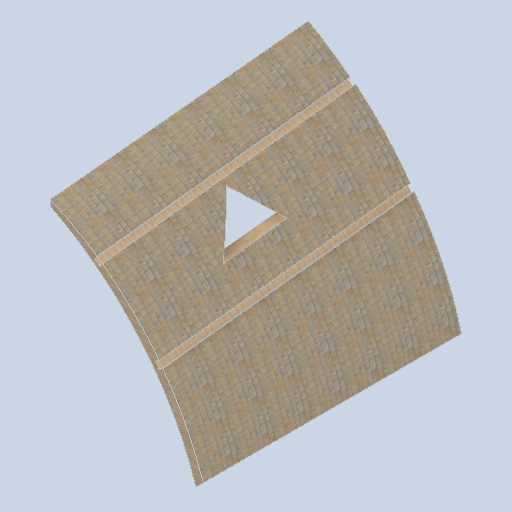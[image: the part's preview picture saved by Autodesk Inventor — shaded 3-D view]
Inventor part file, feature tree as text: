
AUTODESK INVENTOR PART (.ipt)
format: ipt  version: 2024.2 (Build 282272000, 272)  size: 378,368 bytes
history: native  units: in
note: dims shown in document units (in); Inventor stores cm internally (conversion verified against a paired STEP export)
features: other x3, sketch x2, plane x2
ambient origin geometry x8: Origin, YZ Plane, XZ Plane, XY Plane, X Axis, Y Axis, Z Axis, Center Point
bodies: Solid1 (feature_tree)
feature tree (7):
  other  "panel_block_02_MIR.ipt"
  other  "Solid1::panel_block_02_MIR.ipt"
  other  "TaggingFeature1"
  sketch  "Sketch1"  dims[d0=0.3937in]
  sketch  "Sketch2"
  plane  "Work Plane1"
  plane  "Work Plane2"
